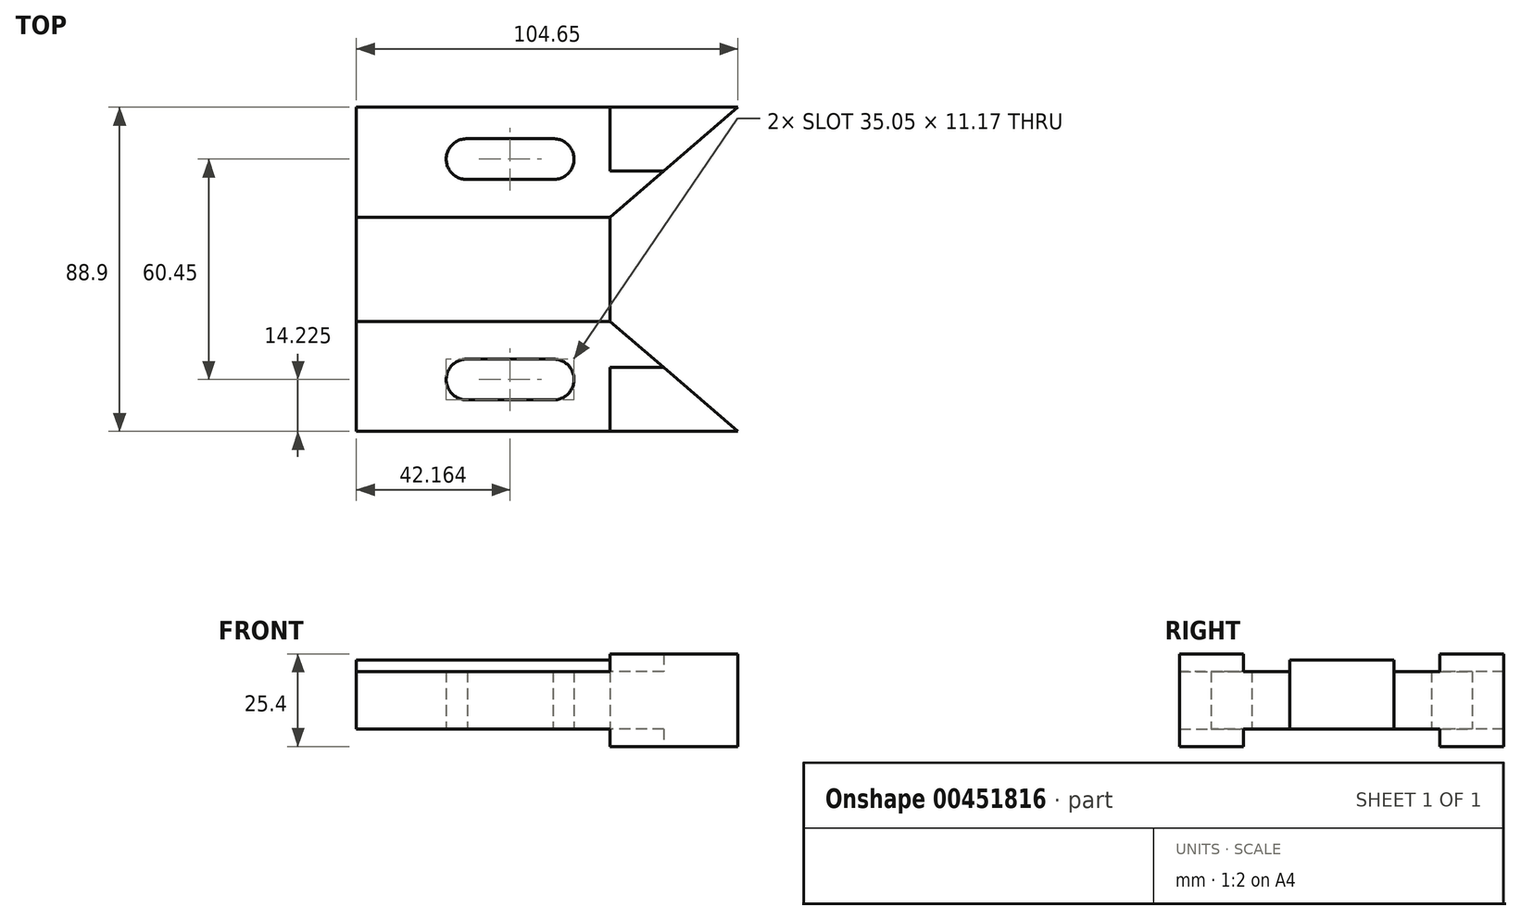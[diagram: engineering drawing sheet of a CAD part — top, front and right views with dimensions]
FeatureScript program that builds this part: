
annotation { "Feature Type Name" : "Feature", "Feature Type Description" : "" }
export const myFeature = defineFeature(function(context is Context, id is Id, definition is map)
    precondition{}
    {
        {
            var Q0;
            Q0=qCreatedBy(makeId("Top.planeOp"),FACE);
            var sketch = newSketch(context, id + "F0", { "sketchPlane" : qUnion([Q0])});
            skLineSegment(sketch, "E0", {"start": v(0, 44.45) * mm, "end": v(0, -44.45) * mm});
            skLineSegment(sketch, "E1", {"start": v(0, -44.45) * mm, "end": v(104.65, -44.45) * mm});
            skLineSegment(sketch, "E2", {"start": v(104.65, -44.45) * mm, "end": v(69.6, -14.29) * mm});
            skLineSegment(sketch, "E3", {"start": v(69.6, -14.29) * mm, "end": v(0, -14.29) * mm});
            skLineSegment(sketch, "E4.MirrorCS", {"start": v(69.6, 14.29) * mm, "end": v(0, 14.29) * mm});
            skLineSegment(sketch, "E5.MirrorCS", {"start": v(0, 44.45) * mm, "end": v(104.65, 44.45) * mm});
            skLineSegment(sketch, "E6.MirrorCS", {"start": v(104.65, 44.45) * mm, "end": v(69.6, 14.29) * mm});
            skLineSegment(sketch, "E7.MirrorCS", {"start": v(0, -44.45) * mm, "end": v(0, 44.45) * mm});
            skLineSegment(sketch, "E8", {"start": v(69.6, 14.29) * mm, "end": v(69.6, -14.29) * mm});
            skLineSegment(sketch, "E9", {"start": v(6.35, 44.45) * mm, "end": v(6.35, 14.29) * mm});
            skLineSegment(sketch, "E10", {"start": v(6.35, -14.29) * mm, "end": v(6.35, -44.45) * mm});
            skArc(sketch, "E11", {"start": v(30.37, 35.81) * mm, "mid": v(24.64, 30.3) * mm, "end": v(30.23, 24.64) * mm});
            skArc(sketch, "E12", {"start": v(54.1, 24.64) * mm, "mid": v(59.69, 30.3) * mm, "end": v(53.95, 35.81) * mm});
            skLineSegment(sketch, "E13", {"start": v(30.37, 35.81) * mm, "end": v(53.95, 35.81) * mm});
            skLineSegment(sketch, "E14", {"start": v(30.23, 24.64) * mm, "end": v(54.1, 24.64) * mm});
            skLineSegment(sketch, "E15.MirrorCS", {"start": v(30.23, -24.64) * mm, "end": v(54.1, -24.64) * mm});
            skArc(sketch, "E16.MirrorCS", {"start": v(54.1, -24.64) * mm, "mid": v(59.69, -30.3) * mm, "end": v(53.95, -35.81) * mm});
            skArc(sketch, "E17.MirrorCS", {"start": v(30.37, -35.81) * mm, "mid": v(24.64, -30.3) * mm, "end": v(30.23, -24.64) * mm});
            skLineSegment(sketch, "E18.MirrorCS", {"start": v(30.37, -35.81) * mm, "end": v(53.95, -35.81) * mm});
            skSolve(sketch);
        }
        {
            var Q0;
            Q0 = qSketchRegion(id + "F0", true);
            extrude(context, id + "F1", {"entities" : qUnion([Q0]), "endBound" : BoundingType.SYMMETRIC, "depth" : 15.75 * mm});
        }
        {
            var Q0;
            Q0=makeQuery(id+"F1.opExtrude","CAP_FACE",FACE,{"disambiguationData":[OSD([sQuery(id+"F0.wireOp",EDGE,"E1"),sQuery(id+"F0.wireOp",EDGE,"E2"),sQuery(id+"F0.wireOp",EDGE,"E5.MirrorCS"),sQuery(id+"F0.wireOp",EDGE,"E6.MirrorCS"),sQuery(id+"F0.wireOp",EDGE,"E7.MirrorCS"),sQuery(id+"F0.wireOp",EDGE,"E8"),sQuery(id+"F0.wireOp",EDGE,"E11"),sQuery(id+"F0.wireOp",EDGE,"E12"),sQuery(id+"F0.wireOp",EDGE,"E13"),sQuery(id+"F0.wireOp",EDGE,"E14"),sQuery(id+"F0.wireOp",EDGE,"E15.MirrorCS"),sQuery(id+"F0.wireOp",EDGE,"E16.MirrorCS"),sQuery(id+"F0.wireOp",EDGE,"E17.MirrorCS"),sQuery(id+"F0.wireOp",EDGE,"E18.MirrorCS")])],"isStart":false});
            var sketch = newSketch(context, id + "F2", { "sketchPlane" : qUnion([Q0])});
            skLineSegment(sketch, "E19", {"start": v(69.6, 14.29) * mm, "end": v(69.6, -14.29) * mm});
            skLineSegment(sketch, "E20", {"start": v(69.6, -14.29) * mm, "end": v(0, -14.29) * mm});
            skLineSegment(sketch, "E21", {"start": v(0, -14.29) * mm, "end": v(0, 14.29) * mm});
            skLineSegment(sketch, "E22", {"start": v(0, 14.29) * mm, "end": v(69.6, 14.29) * mm});
            skSolve(sketch);
        }
        {
            var Q0;
            Q0=makeQuery(id+"F2.imprint","IMPRINT",FACE,{"disambiguationData":[TD([[makeQuery(id+"F2.imprint","IMPRINT",EDGE,{"derivedFrom":sQuery(id+"F2.wireOp",EDGE,"E19")}),-1.0]])]});
            extrude(context, id + "F3", {"entities" : qUnion([Q0]), "operationType" : NewBodyOperationType.ADD, "endBound" : BoundingType.SYMMETRIC, "depth" : 6.35 * mm});
        }
        {
            var Q0;
            Q0=qCreatedBy(makeId("Top.planeOp"),FACE);
            var sketch = newSketch(context, id + "F4", { "sketchPlane" : qUnion([Q0])});
            skLineSegment(sketch, "E23", {"start": v(69.6, 44.45) * mm, "end": v(104.65, 44.45) * mm});
            skLineSegment(sketch, "E24", {"start": v(104.65, 44.45) * mm, "end": v(84.28, 26.92) * mm});
            skLineSegment(sketch, "E25", {"start": v(69.6, 26.92) * mm, "end": v(69.6, 44.45) * mm});
            skLineSegment(sketch, "E26", {"start": v(69.6, 26.92) * mm, "end": v(84.28, 26.92) * mm});
            skPoint(sketch, "E27.orphan", {"position": v(69.6, 39.56) * mm});
            skPoint(sketch, "E28.orphan", {"position": v(69.6, 14.29) * mm});
            skLineSegment(sketch, "E29.MirrorCS", {"start": v(69.6, -26.92) * mm, "end": v(84.28, -26.92) * mm});
            skLineSegment(sketch, "E30.MirrorCS", {"start": v(69.6, -26.92) * mm, "end": v(69.6, -44.45) * mm});
            skLineSegment(sketch, "E31.MirrorCS", {"start": v(69.6, -44.45) * mm, "end": v(104.65, -44.45) * mm});
            skLineSegment(sketch, "E32.MirrorCS", {"start": v(104.65, -44.45) * mm, "end": v(84.28, -26.92) * mm});
            skSolve(sketch);
        }
        {
            var Q0;
            Q0 = qSketchRegion(id + "F4", true);
            extrude(context, id + "F5", {"entities" : qUnion([Q0]), "operationType" : NewBodyOperationType.ADD, "endBound" : BoundingType.SYMMETRIC, "depth" : 25.4 * mm});
        }
    });
